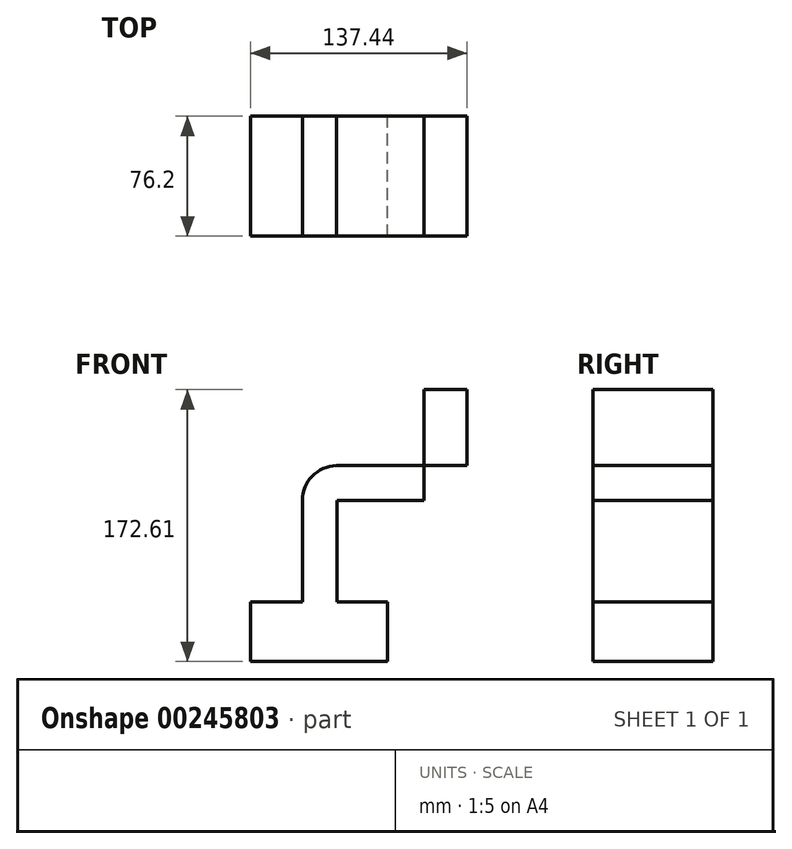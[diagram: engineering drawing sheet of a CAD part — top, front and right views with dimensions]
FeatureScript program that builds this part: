
annotation { "Feature Type Name" : "Feature", "Feature Type Description" : "" }
export const myFeature = defineFeature(function(context is Context, id is Id, definition is map)
    precondition{}
    {
        {
            var Q0;
            Q0=qCreatedBy(makeId("Front.planeOp"),FACE);
            var sketch = newSketch(context, id + "F0", { "sketchPlane" : qUnion([Q0])});
            skLineSegment(sketch, "E0.bottom", {"start": v(846.68, 865.3) * mm, "end": v(867.02, 846.06) * mm});
            skLineSegment(sketch, "E0.left", {"start": v(846.68, 865.3) * mm, "end": v(851.47, 884.78) * mm});
            skLineSegment(sketch, "E1.bottom", {"start": v(-43.44, -39.42) * mm, "end": v(-21.32, -39.42) * mm});
            skLineSegment(sketch, "E1.top", {"start": v(-43.44, 25.34) * mm, "end": v(-21.32, 25.34) * mm});
            skLineSegment(sketch, "E1.left", {"start": v(-43.44, -39.42) * mm, "end": v(-43.44, 25.34) * mm});
            skLineSegment(sketch, "E1.right", {"start": v(-21.32, -39.42) * mm, "end": v(-21.32, 25.34) * mm});
            skArc(sketch, "E2", {"start": v(-21.72, 47.46) * mm, "mid": v(-37.1, 40.84) * mm, "end": v(-43.44, 25.34) * mm});
            skLineSegment(sketch, "E3.bottom", {"start": v(-21.72, 47.46) * mm, "end": v(33.78, 47.46) * mm});
            skLineSegment(sketch, "E3.top", {"start": v(-21.72, 25.34) * mm, "end": v(33.78, 25.34) * mm});
            skLineSegment(sketch, "E3.left", {"start": v(-21.72, 47.46) * mm, "end": v(-21.72, 25.34) * mm});
            skLineSegment(sketch, "E3.right", {"start": v(33.78, 47.46) * mm, "end": v(33.78, 25.34) * mm});
            skArc(sketch, "E4", {"start": v(33.78, 25.34) * mm, "mid": v(50.09, 32.63) * mm, "end": v(61.13, 46.66) * mm});
            skLineSegment(sketch, "E5.bottom", {"start": v(33.78, 47.46) * mm, "end": v(61.13, 47.46) * mm});
            skLineSegment(sketch, "E5.top", {"start": v(33.78, 95.73) * mm, "end": v(61.13, 95.73) * mm});
            skLineSegment(sketch, "E5.left", {"start": v(33.78, 47.46) * mm, "end": v(33.78, 95.73) * mm});
            skLineSegment(sketch, "E5.right", {"start": v(61.13, 47.46) * mm, "end": v(61.13, 95.73) * mm});
            skLineSegment(sketch, "E6.bottom", {"start": v(-76.31, -39.15) * mm, "end": v(10.51, -39.15) * mm});
            skLineSegment(sketch, "E6.top", {"start": v(-76.31, -76.88) * mm, "end": v(10.51, -76.88) * mm});
            skLineSegment(sketch, "E6.left", {"start": v(-76.31, -39.15) * mm, "end": v(-76.31, -76.88) * mm});
            skLineSegment(sketch, "E6.right", {"start": v(10.51, -39.15) * mm, "end": v(10.51, -76.88) * mm});
            skSolve(sketch);
        }
        {
            var Q0;
            Q0 = qSketchRegion(id + "F0", true);
            extrude(context, id + "F1", {"entities" : qUnion([Q0]), "depth" : 76.2 * mm});
        }
    });
